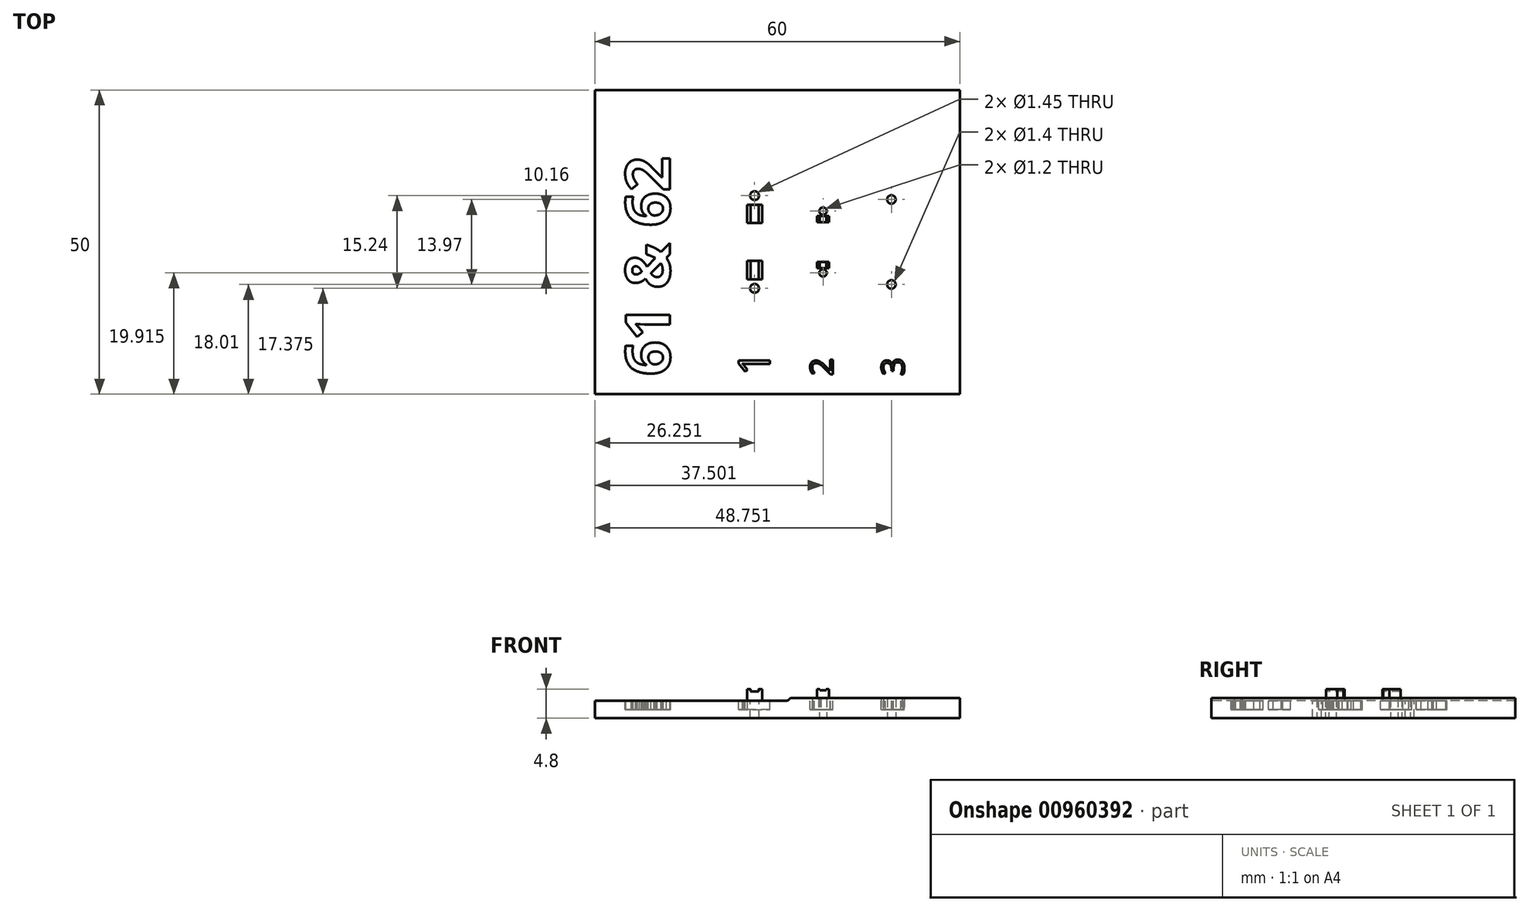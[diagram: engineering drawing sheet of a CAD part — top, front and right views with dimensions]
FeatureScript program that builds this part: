
annotation { "Feature Type Name" : "Feature", "Feature Type Description" : "" }
export const myFeature = defineFeature(function(context is Context, id is Id, definition is map)
    precondition{}
    {
        {
            var Q0;
            Q0=qCreatedBy(makeId("Top.planeOp"),FACE);
            var sketch = newSketch(context, id + "F0", { "sketchPlane" : qUnion([Q0])});
            skLineSegment(sketch, "E0.bottom", {"start": v(-43.16, 28.34) * mm, "end": v(16.84, 28.34) * mm});
            skLineSegment(sketch, "E0.top", {"start": v(-43.16, -21.66) * mm, "end": v(16.84, -21.66) * mm});
            skLineSegment(sketch, "E0.left", {"start": v(-43.16, 28.34) * mm, "end": v(-43.16, -21.66) * mm});
            skLineSegment(sketch, "E0.right", {"start": v(16.84, 28.34) * mm, "end": v(16.84, -21.66) * mm});
            skSolve(sketch);
        }
        {
            var Q0;
            Q0=makeQuery(id+"F0.imprint","IMPRINT",FACE,{"disambiguationData":[TD([[makeQuery(id+"F0.imprint","IMPRINT",EDGE,{"derivedFrom":sQuery(id+"F0.wireOp",EDGE,"E0.bottom")}),-1.0]])]});
            extrude(context, id + "F1", {"entities" : qUnion([Q0]), "depth" : 2.9 * mm, "offsetDistance" : 25 * mm});
        }
        {
            var Q0;
            Q0=makeQuery(id+"F1.opExtrude","CAP_FACE",FACE,{"disambiguationData":[OSD([sQuery(id+"F0.wireOp",EDGE,"E0.bottom"),sQuery(id+"F0.wireOp",EDGE,"E0.top"),sQuery(id+"F0.wireOp",EDGE,"E0.left"),sQuery(id+"F0.wireOp",EDGE,"E0.right")])],"isStart":false});
            var sketch = newSketch(context, id + "F2", { "sketchPlane" : qUnion([Q0])});
            skText(sketch, "E1", { "text": "61 & 62", "fontName": "OpenSans-Bold.ttf"});
            skText(sketch, "E2", { "text": "1", "fontName": "OpenSans-Regular.ttf"});
            skText(sketch, "E3", { "text": "2", "fontName": "OpenSans-Regular.ttf"});
            skText(sketch, "E4", { "text": "3", "fontName": "OpenSans-Regular.ttf"});
            const initialGuessF2  = {"E1": [-0.03084, -0.01866, 0, 1, 0.00731], "E2": [-0.01436, -0.01866, 0, 1, 0.00522], "E3": [-0.00407, -0.01866, 0, 1, 0.0037], "E4": [0.00768, -0.01866, 0, 1, 0.00374]};
            skSetInitialGuess(sketch, initialGuessF2);
            skSolve(sketch);
        }
        {
            var Q0;
            Q0=qSketchRegion(id+"F2",true);
            extrude(context, id + "F3", {"entities" : qUnion([Q0]), "operationType" : NewBodyOperationType.REMOVE, "oppositeDirection" : true, "depth" : 1.5 * mm, "offsetDistance" : 25 * mm});
        }
        {
            var Q0;
            {var subQ0=sQuery(id+"F0.wireOp",EDGE,"E0.left");var subQ1=sQuery(id+"F0.wireOp",EDGE,"E0.bottom");var subQ2=sQuery(id+"F0.wireOp",EDGE,"E0.right");var subQ3=sQuery(id+"F0.wireOp",EDGE,"E0.top");Q0=makeQuery(id+"F3.boolean.opBoolean","SPLIT",FACE,{"disambiguationData":[TD([makeQuery(id+"F1.opExtrude","SWEPT_FACE",FACE,{"disambiguationData":[OSD([subQ1])]})])],"derivedFrom":makeQuery(id+"F1.opExtrude","CAP_FACE",FACE,{"disambiguationData":[OSD([subQ1,subQ3,subQ0,subQ2])],"isStart":false})});}
            var sketch = newSketch(context, id + "F4", { "sketchPlane" : qUnion([Q0])});
            skCircle(sketch, "E5", {"center": v(-16.9, -4.28) * mm, "radius": 0.72 * mm});
            skCircle(sketch, "E6", {"center": v(-16.9, 10.96) * mm, "radius": 0.72 * mm});
            skLineSegment(sketch, "E7.bottom", {"start": v(-18.16, -2.78) * mm, "end": v(-15.66, -2.78) * mm});
            skLineSegment(sketch, "E7.top", {"start": v(-18.16, 0.22) * mm, "end": v(-15.66, 0.22) * mm});
            skLineSegment(sketch, "E7.left", {"start": v(-18.16, -2.78) * mm, "end": v(-18.16, 0.22) * mm});
            skLineSegment(sketch, "E7.right", {"start": v(-15.66, -2.78) * mm, "end": v(-15.66, 0.22) * mm});
            skCircle(sketch, "E8", {"center": v(-16.9, 3.34) * mm, "radius": 2.25 * mm});
            skLineSegment(sketch, "E9.bottom", {"start": v(-18.16, 6.46) * mm, "end": v(-15.66, 6.46) * mm});
            skLineSegment(sketch, "E9.top", {"start": v(-18.16, 9.46) * mm, "end": v(-15.66, 9.46) * mm});
            skLineSegment(sketch, "E9.left", {"start": v(-18.16, 6.46) * mm, "end": v(-18.16, 9.46) * mm});
            skLineSegment(sketch, "E9.right", {"start": v(-15.66, 6.46) * mm, "end": v(-15.66, 9.46) * mm});
            skCircle(sketch, "E10", {"center": v(-5.66, -1.74) * mm, "radius": 0.6 * mm});
            skCircle(sketch, "E11", {"center": v(-5.66, 8.42) * mm, "radius": 0.6 * mm});
            skLineSegment(sketch, "E12.bottom", {"start": v(-6.66, -0.94) * mm, "end": v(-4.66, -0.94) * mm});
            skLineSegment(sketch, "E12.top", {"start": v(-6.66, 0.06) * mm, "end": v(-4.66, 0.06) * mm});
            skLineSegment(sketch, "E12.left", {"start": v(-6.66, -0.94) * mm, "end": v(-6.66, 0.06) * mm});
            skLineSegment(sketch, "E12.right", {"start": v(-4.66, -0.94) * mm, "end": v(-4.66, 0.06) * mm});
            skLineSegment(sketch, "E13.bottom", {"start": v(-6.66, 6.62) * mm, "end": v(-4.66, 6.62) * mm});
            skLineSegment(sketch, "E13.top", {"start": v(-6.66, 7.62) * mm, "end": v(-4.66, 7.62) * mm});
            skLineSegment(sketch, "E13.left", {"start": v(-6.66, 6.62) * mm, "end": v(-6.66, 7.62) * mm});
            skLineSegment(sketch, "E13.right", {"start": v(-4.66, 6.62) * mm, "end": v(-4.66, 7.62) * mm});
            skCircle(sketch, "E14", {"center": v(5.6, -3.65) * mm, "radius": 0.7 * mm});
            skCircle(sketch, "E15", {"center": v(5.6, 10.32) * mm, "radius": 0.7 * mm});
            skLineSegment(sketch, "E16", {"start": v(-11.28, -21.66) * mm, "end": v(-11.28, 28.34) * mm});
            skLineSegment(sketch, "E17.bottom", {"start": v(-17.56, 9.46) * mm, "end": v(-16.26, 9.46) * mm});
            skLineSegment(sketch, "E17.top", {"start": v(-17.56, 6.46) * mm, "end": v(-16.26, 6.46) * mm});
            skLineSegment(sketch, "E17.left", {"start": v(-17.56, 9.46) * mm, "end": v(-17.56, 6.46) * mm});
            skLineSegment(sketch, "E17.right", {"start": v(-16.26, 9.46) * mm, "end": v(-16.26, 6.46) * mm});
            skLineSegment(sketch, "E18.bottom", {"start": v(-17.56, 0.22) * mm, "end": v(-16.26, 0.22) * mm});
            skLineSegment(sketch, "E18.top", {"start": v(-17.56, -2.78) * mm, "end": v(-16.26, -2.78) * mm});
            skLineSegment(sketch, "E18.left", {"start": v(-17.56, 0.22) * mm, "end": v(-17.56, -2.78) * mm});
            skLineSegment(sketch, "E18.right", {"start": v(-16.26, 0.22) * mm, "end": v(-16.26, -2.78) * mm});
            skLineSegment(sketch, "E19.bottom", {"start": v(-6.2, 7.62) * mm, "end": v(-5.1, 7.62) * mm});
            skLineSegment(sketch, "E19.top", {"start": v(-6.2, 6.62) * mm, "end": v(-5.1, 6.62) * mm});
            skLineSegment(sketch, "E19.left", {"start": v(-6.2, 7.62) * mm, "end": v(-6.2, 6.62) * mm});
            skLineSegment(sketch, "E19.right", {"start": v(-5.1, 7.62) * mm, "end": v(-5.1, 6.62) * mm});
            skLineSegment(sketch, "E20.bottom", {"start": v(-6.2, 0.06) * mm, "end": v(-5.1, 0.06) * mm});
            skLineSegment(sketch, "E20.top", {"start": v(-6.2, -0.94) * mm, "end": v(-5.1, -0.94) * mm});
            skLineSegment(sketch, "E20.left", {"start": v(-6.2, 0.06) * mm, "end": v(-6.2, -0.94) * mm});
            skLineSegment(sketch, "E20.right", {"start": v(-5.1, 0.06) * mm, "end": v(-5.1, -0.94) * mm});
            skSolve(sketch);
        }
        {
            var Q0;
            Q0=makeQuery(id+"F4.imprint","IMPRINT",FACE,{"disambiguationData":[TD([[makeQuery(id+"F4.imprint","IMPRINT",EDGE,{"derivedFrom":sQuery(id+"F4.wireOp",EDGE,"E5")}),1.0]])]});
            var Q1;
            Q1=makeQuery(id+"F4.imprint","IMPRINT",FACE,{"disambiguationData":[TD([[makeQuery(id+"F4.imprint","IMPRINT",EDGE,{"derivedFrom":sQuery(id+"F4.wireOp",EDGE,"E6")}),1.0]])]});
            extrude(context, id + "F5", {"entities" : qUnion([Q0, Q1]), "operationType" : NewBodyOperationType.REMOVE, "endBound" : BoundingType.UP_TO_NEXT, "oppositeDirection" : true, "depth" : 25 * mm, "offsetDistance" : 25 * mm});
        }
        {
            var Q0;
            {var subQ0=sQuery(id+"F4.wireOp",EDGE,"E7.right");var subQ5=sQuery(id+"F4.wireOp",EDGE,"E7.left");Q0=qUnion([makeQuery(id+"F4.imprint","IMPRINT",FACE,{"disambiguationData":[TD([[makeQuery(id+"F4.imprint","IMPRINT",EDGE,{"derivedFrom":subQ5}),-1.0]])]}),makeQuery(id+"F4.imprint","IMPRINT",FACE,{"disambiguationData":[TD([[makeQuery(id+"F4.imprint","IMPRINT",EDGE,{"derivedFrom":subQ0}),1.0]])]})]);}
            var Q1;
            {var subQ0=sQuery(id+"F4.wireOp",EDGE,"E9.right");var subQ5=sQuery(id+"F4.wireOp",EDGE,"E9.left");Q1=qUnion([makeQuery(id+"F4.imprint","IMPRINT",FACE,{"disambiguationData":[TD([[makeQuery(id+"F4.imprint","IMPRINT",EDGE,{"derivedFrom":subQ5}),-1.0]])]}),makeQuery(id+"F4.imprint","IMPRINT",FACE,{"disambiguationData":[TD([[makeQuery(id+"F4.imprint","IMPRINT",EDGE,{"derivedFrom":subQ0}),1.0]])]})]);}
            extrude(context, id + "F6", {"entities" : qUnion([Q0, Q1]), "operationType" : NewBodyOperationType.ADD, "depth" : 1.9 * mm, "offsetDistance" : 25 * mm});
        }
        {
            var Q0;
            Q0=makeQuery(id+"F4.imprint","IMPRINT",FACE,{"disambiguationData":[TD([[makeQuery(id+"F4.imprint","IMPRINT",EDGE,{"derivedFrom":sQuery(id+"F4.wireOp",EDGE,"E10")}),-1.0]])]});
            extrude(context, id + "F7", {"entities" : qUnion([Q0]), "operationType" : NewBodyOperationType.ADD, "depth" : 0.4 * mm, "offsetDistance" : 25 * mm});
        }
        {
            var Q0;
            Q0=makeQuery(id+"F4.imprint","IMPRINT",FACE,{"disambiguationData":[TD([[makeQuery(id+"F4.imprint","IMPRINT",EDGE,{"derivedFrom":sQuery(id+"F4.wireOp",EDGE,"E11")}),1.0]])]});
            var Q1;
            Q1=makeQuery(id+"F4.imprint","IMPRINT",FACE,{"disambiguationData":[TD([[makeQuery(id+"F4.imprint","IMPRINT",EDGE,{"derivedFrom":sQuery(id+"F4.wireOp",EDGE,"E14")}),1.0]])]});
            var Q2;
            Q2=makeQuery(id+"F4.imprint","IMPRINT",FACE,{"disambiguationData":[TD([[makeQuery(id+"F4.imprint","IMPRINT",EDGE,{"derivedFrom":sQuery(id+"F4.wireOp",EDGE,"E15")}),1.0]])]});
            var Q3;
            Q3=makeQuery(id+"F4.imprint","IMPRINT",FACE,{"disambiguationData":[TD([[makeQuery(id+"F4.imprint","IMPRINT",EDGE,{"derivedFrom":sQuery(id+"F4.wireOp",EDGE,"E10")}),1.0]])]});
            extrude(context, id + "F8", {"entities" : qUnion([Q0, Q1, Q2, Q3]), "operationType" : NewBodyOperationType.REMOVE, "endBound" : BoundingType.UP_TO_NEXT, "oppositeDirection" : true, "depth" : 25 * mm, "offsetDistance" : 25 * mm});
        }
        {
            var Q0;
            {var subQ2=sQuery(id+"F4.wireOp",EDGE,"E13.left");var subQ4=sQuery(id+"F4.wireOp",EDGE,"E13.right");Q0=qUnion([makeQuery(id+"F4.imprint","IMPRINT",FACE,{"disambiguationData":[TD([[makeQuery(id+"F4.imprint","IMPRINT",EDGE,{"derivedFrom":subQ4}),1.0]])]}),makeQuery(id+"F4.imprint","IMPRINT",FACE,{"disambiguationData":[TD([[makeQuery(id+"F4.imprint","IMPRINT",EDGE,{"derivedFrom":subQ2}),-1.0]])]})]);}
            var Q1;
            {var subQ0=sQuery(id+"F4.wireOp",EDGE,"E12.right");var subQ5=sQuery(id+"F4.wireOp",EDGE,"E12.left");Q1=qUnion([makeQuery(id+"F4.imprint","IMPRINT",FACE,{"disambiguationData":[TD([[makeQuery(id+"F4.imprint","IMPRINT",EDGE,{"derivedFrom":subQ5}),-1.0]])]}),makeQuery(id+"F4.imprint","IMPRINT",FACE,{"disambiguationData":[TD([[makeQuery(id+"F4.imprint","IMPRINT",EDGE,{"derivedFrom":subQ0}),1.0]])]})]);}
            extrude(context, id + "F9", {"entities" : qUnion([Q0, Q1]), "operationType" : NewBodyOperationType.ADD, "depth" : 1.9 * mm, "offsetDistance" : 25 * mm});
        }
        {
            var Q0;
            {var subQ0=sQuery(id+"F4.wireOp",EDGE,"E17.left");Q0=makeQuery(id+"F4.imprint","IMPRINT",FACE,{"disambiguationData":[TD([[makeQuery(id+"F4.imprint","IMPRINT",EDGE,{"derivedFrom":subQ0}),1.0]])]});}
            var Q1;
            {var subQ0=sQuery(id+"F4.wireOp",EDGE,"E18.left");Q1=makeQuery(id+"F4.imprint","IMPRINT",FACE,{"disambiguationData":[TD([[makeQuery(id+"F4.imprint","IMPRINT",EDGE,{"derivedFrom":subQ0}),1.0]])]});}
            extrude(context, id + "F10", {"entities" : qUnion([Q0, Q1]), "operationType" : NewBodyOperationType.ADD, "depth" : 1.5 * mm, "offsetDistance" : 25 * mm});
        }
        {
            var Q0;
            Q0=makeQuery(id+"F6.opExtrude","CAP_EDGE",EDGE,{"disambiguationData":[OSD([sQuery(id+"F4.wireOp",EDGE,"E17.right")])],"isStart":false});
            var Q1;
            Q1=makeQuery(id+"F6.opExtrude","CAP_EDGE",EDGE,{"disambiguationData":[OSD([sQuery(id+"F4.wireOp",EDGE,"E17.left")])],"isStart":false});
            var Q2;
            Q2=makeQuery(id+"F6.opExtrude","CAP_EDGE",EDGE,{"disambiguationData":[OSD([sQuery(id+"F4.wireOp",EDGE,"E18.left")])],"isStart":false});
            var Q3;
            Q3=makeQuery(id+"F6.opExtrude","CAP_EDGE",EDGE,{"disambiguationData":[OSD([sQuery(id+"F4.wireOp",EDGE,"E18.right")])],"isStart":false});
            var Q4;
            Q4=makeQuery(id+"F9.opExtrude","CAP_EDGE",EDGE,{"disambiguationData":[OSD([sQuery(id+"F4.wireOp",EDGE,"E19.left")])],"isStart":false});
            var Q5;
            Q5=makeQuery(id+"F9.opExtrude","CAP_EDGE",EDGE,{"disambiguationData":[OSD([sQuery(id+"F4.wireOp",EDGE,"E19.right")])],"isStart":false});
            var Q6;
            Q6=makeQuery(id+"F9.opExtrude","CAP_EDGE",EDGE,{"disambiguationData":[OSD([sQuery(id+"F4.wireOp",EDGE,"E20.left")])],"isStart":false});
            var Q7;
            Q7=makeQuery(id+"F9.opExtrude","CAP_EDGE",EDGE,{"disambiguationData":[OSD([sQuery(id+"F4.wireOp",EDGE,"E20.right")])],"isStart":false});
            fillet(context, id + "F11", {"entities" : qUnion([Q0, Q1, Q2, Q3, Q4, Q5, Q6, Q7]), "radius" : 0.1 * mm, "tangentPropagation" : true, "allowEdgeOverflow" : false});
        }
        {
            var Q0;
            {var subQ0=sQuery(id+"F4.wireOp",EDGE,"E20.left");Q0=makeQuery(id+"F4.imprint","IMPRINT",FACE,{"disambiguationData":[TD([[makeQuery(id+"F4.imprint","IMPRINT",EDGE,{"derivedFrom":subQ0}),1.0]])]});}
            var Q1;
            {var subQ0=sQuery(id+"F4.wireOp",EDGE,"E19.left");Q1=makeQuery(id+"F4.imprint","IMPRINT",FACE,{"disambiguationData":[TD([[makeQuery(id+"F4.imprint","IMPRINT",EDGE,{"derivedFrom":subQ0}),1.0]])]});}
            extrude(context, id + "F12", {"entities" : qUnion([Q0, Q1]), "operationType" : NewBodyOperationType.ADD, "depth" : 1.7 * mm, "offsetDistance" : 25 * mm});
        }
        {
            var Q0;
            Q0=makeQuery(id+"F7.opExtrude","CAP_EDGE",EDGE,{"disambiguationData":[OSD([sQuery(id+"F4.wireOp",EDGE,"E16")])],"isStart":false});
            fillet(context, id + "F13", {"entities" : qUnion([Q0]), "radius" : 0.4 * mm, "tangentPropagation" : true, "allowEdgeOverflow" : false});
        }
        {
            var Q0;
            {var subQ32=sQuery(id+"F0.wireOp",EDGE,"E0.bottom");var subQ33=makeQuery(id+"F1.opExtrude","SWEPT_FACE",FACE,{"disambiguationData":[OSD([subQ32])]});var subQ38=sQuery(id+"F0.wireOp",EDGE,"E0.top");var subQ46=sQuery(id+"F0.wireOp",EDGE,"E0.left");var subQ56=sQuery(id+"F4.wireOp",EDGE,"E16");var subQ88=sQuery(id+"F0.wireOp",EDGE,"E0.right");Q0=makeQuery(id+"F13.opFillet","BLEND_EDGE",EDGE,{"blendedFrom":[makeQuery(id+"F7.opExtrude","CAP_EDGE",EDGE,{"disambiguationData":[OSD([subQ56])],"isStart":false}),makeQuery(id+"F7.boolean.opBoolean","SPLIT",FACE,{"disambiguationData":[TD([subQ33])],"derivedFrom":makeQuery(id+"F3.boolean.opBoolean","SPLIT",FACE,{"disambiguationData":[TD([subQ33])],"derivedFrom":makeQuery(id+"F1.opExtrude","CAP_FACE",FACE,{"disambiguationData":[OSD([subQ32,subQ38,subQ46,subQ88])],"isStart":false})})})],"blendedInto":[makeQuery(id+"F7.boolean.opBoolean","SPLIT",FACE,{"disambiguationData":[TD([subQ33])],"derivedFrom":makeQuery(id+"F3.boolean.opBoolean","SPLIT",FACE,{"disambiguationData":[TD([subQ33])],"derivedFrom":makeQuery(id+"F1.opExtrude","CAP_FACE",FACE,{"disambiguationData":[OSD([subQ32,subQ38,subQ46,subQ88])],"isStart":false})})})]});}
            fillet(context, id + "F14", {"entities" : qUnion([Q0]), "radius" : 0.4 * mm, "tangentPropagation" : true, "allowEdgeOverflow" : false});
        }
    });
